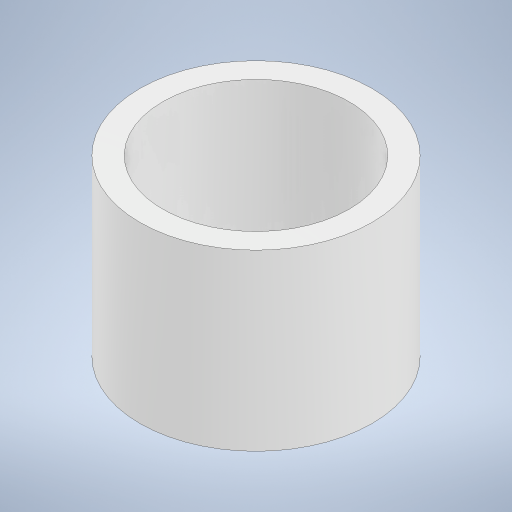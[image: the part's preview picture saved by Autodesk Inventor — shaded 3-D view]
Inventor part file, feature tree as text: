
AUTODESK INVENTOR PART (.ipt)
format: ipt  version: 2024 (Build 280153000, 153)  size: 271,360 bytes
history: native  units: in
note: dims shown in document units (in); Inventor stores cm internally (conversion verified against a paired STEP export)
features: other x1, extrude x1
ambient origin geometry x8: Origin, YZ Plane, XZ Plane, XY Plane, X Axis, Y Axis, Z Axis, Center Point
bodies: Body1 (feature_tree)
feature tree (2):
  other  "Sólido1"
  extrude  "Extrusión1"  Depth=1.0492in
